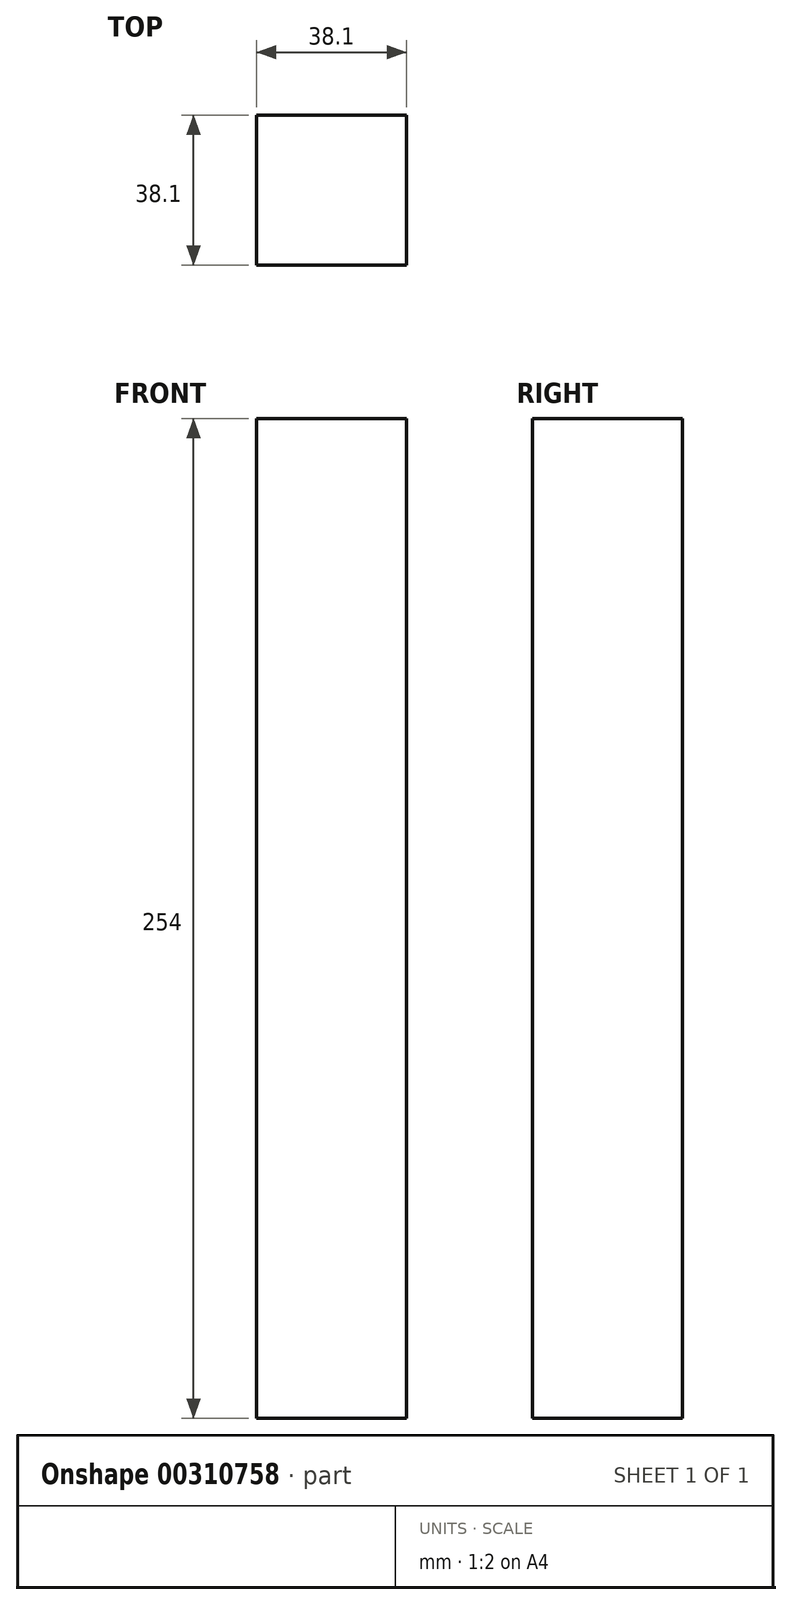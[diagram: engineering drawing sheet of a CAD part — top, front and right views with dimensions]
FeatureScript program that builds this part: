
annotation { "Feature Type Name" : "Feature", "Feature Type Description" : "" }
export const myFeature = defineFeature(function(context is Context, id is Id, definition is map)
    precondition{}
    {
        {
            var Q0;
            Q0=qCreatedBy(makeId("Top.planeOp"),FACE);
            var sketch = newSketch(context, id + "F0", { "sketchPlane" : qUnion([Q0])});
            skLineSegment(sketch, "E0.bottom", {"start": v(0, -3.61) * mm, "end": v(38.1, -3.61) * mm});
            skLineSegment(sketch, "E0.top", {"start": v(0, -41.71) * mm, "end": v(38.1, -41.71) * mm});
            skLineSegment(sketch, "E0.left", {"start": v(0, -3.61) * mm, "end": v(0, -41.71) * mm});
            skLineSegment(sketch, "E0.right", {"start": v(38.1, -3.61) * mm, "end": v(38.1, -41.71) * mm});
            skSolve(sketch);
        }
        {
            var Q0;
            Q0 = qSketchRegion(id + "F0", true);
            extrude(context, id + "F1", {"entities" : qUnion([Q0]), "depth" : 254 * mm, "offsetDistance" : 25.4 * mm});
        }
    });
